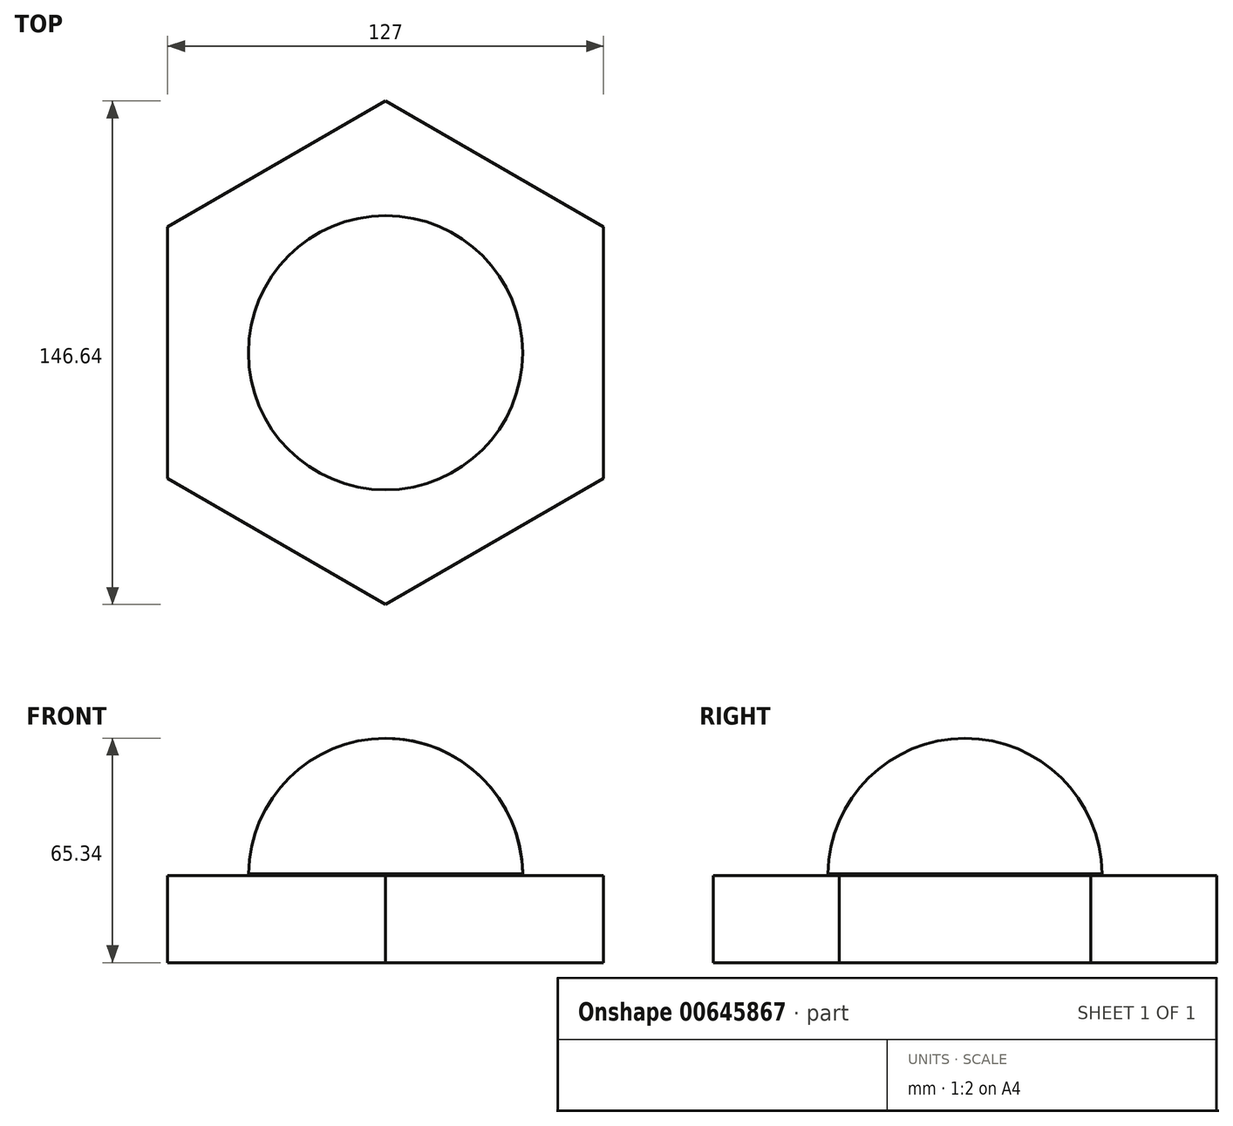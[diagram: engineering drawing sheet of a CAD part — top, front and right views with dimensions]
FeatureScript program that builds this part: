
annotation { "Feature Type Name" : "Feature", "Feature Type Description" : "" }
export const myFeature = defineFeature(function(context is Context, id is Id, definition is map)
    precondition{}
    {
        {
            var Q0;
            Q0=qCreatedBy(makeId("Top.planeOp"),FACE);
            var sketch = newSketch(context, id + "F0", { "sketchPlane" : qUnion([Q0])});
            skCircle(sketch, "E0.cCircle", {"center": v(0, 0) * mm, "radius": 63.5 * mm, "construction": true});
            skLineSegment(sketch, "E0.0", {"start": v(-63.5, 36.66) * mm, "end": v(0, 73.32) * mm});
            skLineSegment(sketch, "E0.1", {"start": v(0, 73.32) * mm, "end": v(63.5, 36.66) * mm});
            skLineSegment(sketch, "E0.2", {"start": v(63.5, 36.66) * mm, "end": v(63.5, -36.66) * mm});
            skLineSegment(sketch, "E0.3", {"start": v(63.5, -36.66) * mm, "end": v(0, -73.32) * mm});
            skLineSegment(sketch, "E0.4", {"start": v(0, -73.32) * mm, "end": v(-63.5, -36.66) * mm});
            skLineSegment(sketch, "E0.5", {"start": v(-63.5, -36.66) * mm, "end": v(-63.5, 36.66) * mm});
            skPoint(sketch, "E0.0.midPoint", {"position": v(-31.75, 55) * mm});
            skSolve(sketch);
        }
        {
            var Q0;
            Q0=makeQuery(id+"F0.imprint","IMPRINT",FACE,{"disambiguationData":[TD([[makeQuery(id+"F0.imprint","IMPRINT",EDGE,{"derivedFrom":sQuery(id+"F0.wireOp",EDGE,"E0.0")}),-1.0]])]});
            extrude(context, id + "F1", {"entities" : qUnion([Q0]), "depth" : 25.4 * mm, "offsetDistance" : 25.4 * mm});
        }
        {
            var Q0;
            Q0=qCreatedBy(makeId("Front.planeOp"),FACE);
            var sketch = newSketch(context, id + "F2", { "sketchPlane" : qUnion([Q0])});
            skArc(sketch, "E1", {"start": v(39.94, 25.85) * mm, "mid": v(28.08, 53.8) * mm, "end": v(0, 65.34) * mm});
            skLineSegment(sketch, "E2", {"start": v(0, 65.34) * mm, "end": v(0, 25.4) * mm});
            skLineSegment(sketch, "E3", {"start": v(39.94, 25.85) * mm, "end": v(0, 25.4) * mm});
            skSolve(sketch);
        }
        {
            var Q0;
            Q0=makeQuery(id+"F2.imprint","IMPRINT",FACE,{"disambiguationData":[TD([[makeQuery(id+"F2.imprint","IMPRINT",EDGE,{"derivedFrom":sQuery(id+"F2.wireOp",EDGE,"E1")}),1.0]])]});
            var Q1;
            Q1=sQuery(id+"F2.wireOp",EDGE,"E2");
            revolve(context, id + "F3", {"operationType" : NewBodyOperationType.ADD, "entities" : qUnion([Q0]), "axis" : qUnion([Q1]), "revolveType" : RevolveType.FULL});
        }
    });
